# Revit family: Hager-Univers-IP30-D161-3rows-Cl.II-FWB_encl_empty-NoHosted-CH-it
name_source: partatom
category: Electrical Equipment
units: mm (PartAtom-declared; Revit-internal decimal feet)

## family parameters
Always vertical = Yes
Cut with Voids When Loaded = No
Panel Configuration = Two Columns, Circuits Across
Part Type = Panelboard
Room Calculation Point = No
Round Connector Dimension = Use Diameter
Shared = No
Work Plane-Based = Yes

## types (1)
- A parete IP30 L300 A500 P161  - FWB31D1
    Default Elevation = 1219 mm
    EF000003 - Tipo di montaggio = EV000384 - A parete
    EF000007 - colore = EV000202 - bianco
    EF000008 - Larghezza = 300 mm
    EF000040 - Altezza = 500 mm  [stored 1.64042 ft]
    EF000049 - profondità = 161 mm  [stored 0.528215 ft]
    EF000116 - numero RAL = 9010
    EF000118 - con piastra di montaggio = No
    EF000218 - profondità di incasso = 0 mm  [stored 0 ft]
    EF000266 - numero di file = 0
    EF000339 - tipo di copertura = EV000494 - senza
    EF000437 - numero di ingressi per conduttori = 4
    EF001088 - possibilità di applicazione = Yes
    EF001131 - profondità interna = 156 mm  [stored 0.511811 ft]
    EF001596 - Attacco Lampada = EV000179 - acciaio
    EF001613 - Integrità del circuito = EV000494 - senza
    EF002950 - Numero moduli DIN = 12
    EF003532 - adatto per uso esterno = No
    EF004293 - resistenza agli urti = EV006815 - IK09
    EF004427 - numero di moduli = 36
    EF004464 - tipo di porta = EV000494 - senza
    EF005474 - grado di protezione (IP) = EV006410 - IP30
    EF006244 - coperchio/porta trasparente = No
    EF006306 - con serratura = No
    EF007800 - adatto per parafulmine = No
    EF008873 - corrente nominale (In) = 125 A
    EF009170 - spessore materiale scatola = 2 mm  [stored 0.00656168 ft]
    EF009171 - spessore materiale porta/coperchio = 2 mm  [stored 0.00656168 ft]
    EF009212 - esecuzione coperchio = EV009916 - con taglio
    EF009554 - numero delle aperture per la piastra della flangia = 2
    EF015940 - Coprire con rilascio di sovrapressione = No
    HG000002 - Con porta = No
    HG000003 - Gamma = Univers
    HG000004 - Codice produttore = FWB31D1
    HG000006 - Ad incasso = No
    HG000009 - Porta doppia a battente = No
    HG000010 - Porte asimmetriche = No
    HG000023 - Custodia a doppia sezione = No
    HG000024 - Altezza della sezione inferiore = 600 mm
    HG000026 - A pavimento = No
    HG000027 - Altezza dello zoccolo = 0 mm  [stored 0 ft]
    Manufacturer = Hager
    Type Comments = Univers

note: [stored X ft] marks values corroborated as IEEE doubles in the binary element streams (Revit-internal decimal feet)

## geometry (parser evidence)
native form markers: Blend x4, Sweep x11
no freeform markers — native parametric forms only
